# Revit family: Interceptor_Oil-Zurn-Z1198
name_source: partatom
category: Plumbing Fixtures
units: mm (PartAtom-declared; Revit-internal decimal feet)

## family parameters
Always vertical = Yes
Cut with Voids When Loaded = No
Maintain Annotation Orientation = No
OmniClass Number = 23.45.30.00
OmniClass Title = Washing and Waste Disposal Equipment
Part Type = Normal
Room Calculation Point = No
Round Connector Dimension = Use Radius
Shared = No
Work Plane-Based = No

## types (11) — shared parameters
Assembly Code = D2090300
CW Connection = No
Default Elevation = 20 "
Description = LARGE CAPACITY OIL INTERCEPTOR W/ OIL LEVEL SENSOR
HW Connection = No
Main Material = Steel - Zurn - Fabricated - Acid resistant Coated
Manufacturer = Zurn Water, LLC
Manufacturer Brand = Zurn
Model = Z1198
Modified Date = 02/20/2026
Product Documentation Link = https://files.zurn.com
Product Installation Sheet URL = https://files.zurn.com
Product Page URL = https://www.zurn.com
Product data URL = https://www.bimobject.com
URL = www.zurn.com
Vent Connection = No
WFU = 1
Waste Connection = Yes
zero-valued in all types: CWFU, HWFU

## per-type parameters (varying)
| type | Approx. Weight (Lbs) | C | D | F | G | J | L | Oil Capacity (Gal) | Pipe Size Inside Radius | Pipe Size Nominal Radius | Pipe Size Outer Radius | Type Comments | Water Capacity (Gal) |
| Z1198-75-3 | 332.00 lb | 22.75 " | 18.5 " | 36 " | 28.625 " | 10 " | 25.75 " | 20.00 L | 1.534 " | 1.5 " | 1.75 " | Z1198-3 Inch Pipe 75 G.P.M. | 65.00 L |
| Z1198-100-3 | 432.00 lb | 27 " | 23 " | 42.75 " | 33.625 " | 15.375 " | 30.125 " | 27.00 L | 1.534 " | 1.5 " | 1.75 " | Z1198-3 Inch Pipe 100 G.P.M. | 110.00 L |
| Z1198-125-3 | 780.00 lb | 30.125 " | 24.5 " | 49.25 " | 40 " | 15.688 " | 36.625 " | 33.00 L | 1.534 " | 1.5 " | 1.75 " | Z1198-3 Inch Pipe 125 G.P.M. | 150.00 L |
| Z1198-150-4 | 888.00 lb | 30.75 " | 25.25 " | 56 " | 41.375 " | 17.313 " | 43.875 " | 40.00 L | 2.013 " | 2 " | 2.25 " | Z1198-4 Inch Pipe 150 G.P.M. | 190.00 L |
| Z1198-200-4 | 1055.00 lb | 35.5 " | 29.875 " | 61 " | 43.625 " | 21.063 " | 46.625 " | 53.00 L | 2.013 " | 2 " | 2.25 " | Z1198-4 Inch Pipe 200 G.P.M. | 265.00 L |
| Z1198-250-5 | 1438.00 lb | 41 " | 36 " | 71 " | 51.375 " | 27.813 " | 56.625 " | 67.00 L | 2.524 " | 2.5 " | 2.782 " | Z1198-5 Inch Pipe 250 G.P.M. | 460.00 L |
| Z1198-300-5 | 1840.00 lb | 46.25 " | 39.625 " | 80 " | 58.375 " | 32 " | 65.625 " | 80.00 L | 2.524 " | 2.5 " | 2.782 " | Z1198-5 Inch Pipe 300 G.P.M. | 660.00 L |
| Z1198-350-6 | 2180.00 lb | 50.5 " | 43.875 " | 87 " | 63.625 " | 35.313 " | 74.125 " | 93.00 L | 3.033 " | 3 " | 3.313 " | Z1198-6 Inch Pipe 350 G.P.M. | 860.00 L |
| Z1198-400-6 | 2536.00 lb | 54.25 " | 47.625 " | 94 " | 67 " | 39.313 " | 79.125 " | 107.00 L | 3.033 " | 3 " | 3.313 " | Z1198-6 Inch Pipe 400 G.P.M. | 1090.00 L |
| Z1198-450-6 | 2816.00 lb | 55.25 " | 48.625 " | 100 " | 72 " | 40.375 " | 85.375 " | 120.00 L | 3.033 " | 3 " | 3.313 " | Z1198-6 Inch Pipe 450 G.P.M. | 1275.00 L |
| Z1198-500-6 | 2970.00 lb | 57.25 " | 51.625 " | 104 " | 74 " | 43.188 " | 88.375 " | 133.00 L | 3.033 " | 3 " | 3.313 " | Z1198-6 Inch Pipe 500 G.P.M. | 1435.00 L |

## geometry (parser evidence)
native form markers: Sweep x5
no freeform markers — native parametric forms only
